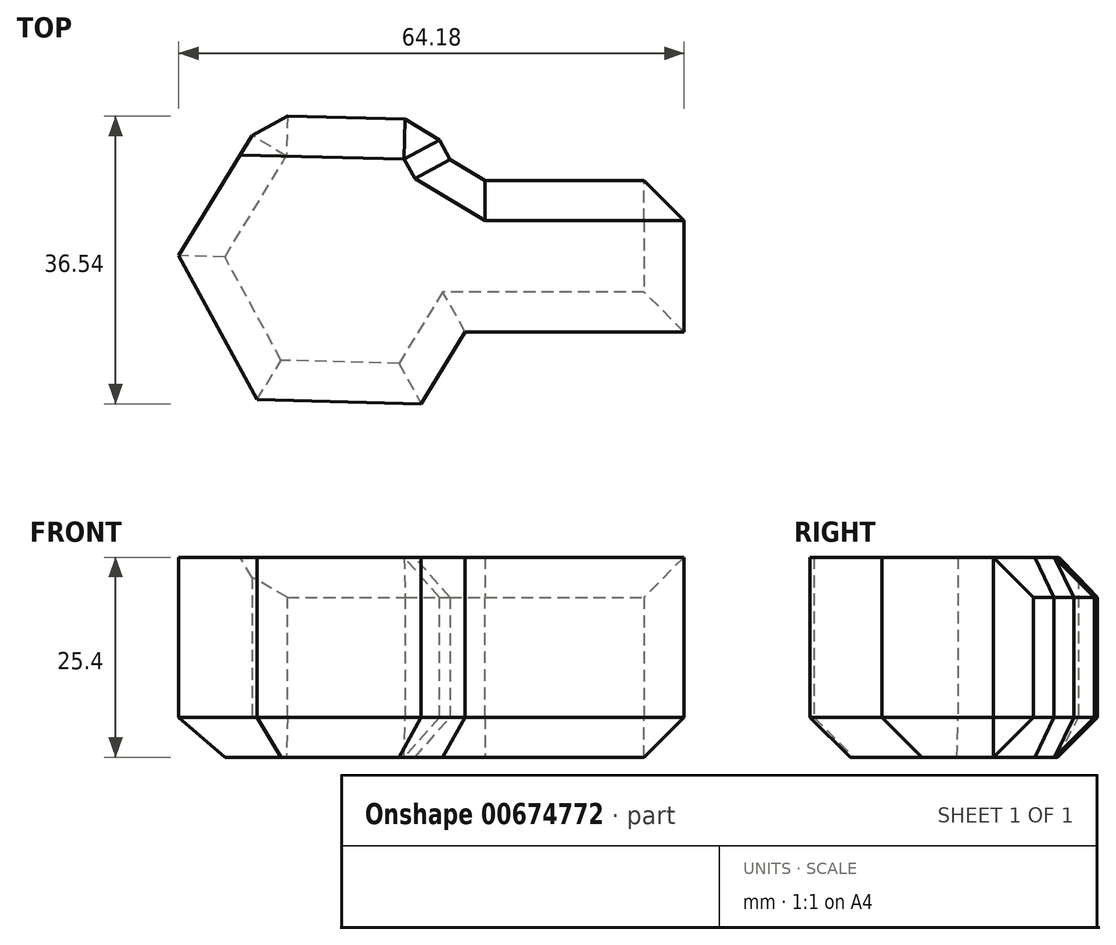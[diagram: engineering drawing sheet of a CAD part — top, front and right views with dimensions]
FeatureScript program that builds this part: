
annotation { "Feature Type Name" : "Feature", "Feature Type Description" : "" }
export const myFeature = defineFeature(function(context is Context, id is Id, definition is map)
    precondition{}
    {
        {
            var Q0;
            Q0=qCreatedBy(makeId("Top.planeOp"),FACE);
            var sketch = newSketch(context, id + "F0", { "sketchPlane" : qUnion([Q0])});
            skCircle(sketch, "E0.cCircle", {"center": v(-46.81, 36.74) * mm, "radius": 18.05 * mm, "construction": true});
            skLineSegment(sketch, "E0.0", {"start": v(-31.26, 27.58) * mm, "end": v(-36.85, 18.43) * mm});
            skLineSegment(sketch, "E0.1", {"start": v(-36.85, 18.43) * mm, "end": v(-57.68, 18.95) * mm});
            skLineSegment(sketch, "E0.2", {"start": v(-57.68, 18.95) * mm, "end": v(-67.65, 37.26) * mm});
            skLineSegment(sketch, "E0.3", {"start": v(-67.65, 37.26) * mm, "end": v(-56.78, 55.04) * mm});
            skLineSegment(sketch, "E0.4", {"start": v(-56.78, 55.04) * mm, "end": v(-35.95, 54.52) * mm});
            skLineSegment(sketch, "E0.5", {"start": v(-35.95, 54.52) * mm, "end": v(-30.96, 45.37) * mm});
            skPoint(sketch, "E0.0.midPoint", {"position": v(-31.41, 27.32) * mm});
            skLineSegment(sketch, "E1.bottom", {"start": v(-31.75, 46.8) * mm, "end": v(-3.47, 46.8) * mm});
            skLineSegment(sketch, "E1.top", {"start": v(-31.75, 27.58) * mm, "end": v(-3.47, 27.58) * mm});
            skLineSegment(sketch, "E1.left", {"start": v(-31.75, 46.8) * mm, "end": v(-31.75, 46.67) * mm});
            skLineSegment(sketch, "E1.right", {"start": v(-3.47, 46.8) * mm, "end": v(-3.47, 27.58) * mm});
            skPoint(sketch, "E2.orphan", {"position": v(-25.98, 36.22) * mm});
            skSolve(sketch);
        }
        {
            var Q0;
            Q0 = qSketchRegion(id + "F0", true);
            extrude(context, id + "F1", {"entities" : qUnion([Q0]), "depth" : 25.4 * mm, "offsetDistance" : 25.4 * mm});
        }
        {
            var Q0;
            Q0=makeQuery(id+"F1.opExtrude","SWEPT_FACE",FACE,{"disambiguationData":[OSD([sQuery(id+"F0.wireOp",EDGE,"E0.4")])]});
            var Q1;
            Q1=makeQuery(id+"F1.opExtrude","SWEPT_FACE",FACE,{"disambiguationData":[OSD([sQuery(id+"F0.wireOp",EDGE,"E0.5")])]});
            var Q2;
            Q2=makeQuery(id+"F1.opExtrude","CAP_EDGE",EDGE,{"disambiguationData":[OSD([sQuery(id+"F0.wireOp",EDGE,"E0.5")])],"isStart":false});
            var Q3;
            Q3=makeQuery(id+"F1.opExtrude","CAP_FACE",FACE,{"disambiguationData":[OSD([sQuery(id+"F0.wireOp",EDGE,"E0.0"),sQuery(id+"F0.wireOp",EDGE,"E0.1"),sQuery(id+"F0.wireOp",EDGE,"E0.2"),sQuery(id+"F0.wireOp",EDGE,"E0.3"),sQuery(id+"F0.wireOp",EDGE,"E0.4"),sQuery(id+"F0.wireOp",EDGE,"E0.5"),sQuery(id+"F0.wireOp",EDGE,"E1.bottom"),sQuery(id+"F0.wireOp",EDGE,"E1.top"),sQuery(id+"F0.wireOp",EDGE,"E1.right")])],"isStart":true});
            var Q4;
            Q4=makeQuery(id+"F1.opExtrude","SWEPT_EDGE",EDGE,{"disambiguationData":[OSD([sQuery(id+"F0.wireOp",EDGE,"E0.4"),sQuery(id+"F0.wireOp",EDGE,"E0.5")])]});
            var Q5;
            Q5=makeQuery(id+"F1.opExtrude","CAP_EDGE",EDGE,{"disambiguationData":[OSD([sQuery(id+"F0.wireOp",EDGE,"E0.4")])],"isStart":false});
            var Q6;
            Q6=makeQuery(id+"F1.opExtrude","CAP_EDGE",EDGE,{"disambiguationData":[OSD([sQuery(id+"F0.wireOp",EDGE,"E0.5")])],"isStart":true});
            var Q7;
            Q7=makeQuery(id+"F1.opExtrude","CAP_EDGE",EDGE,{"disambiguationData":[OSD([sQuery(id+"F0.wireOp",EDGE,"E0.4")])],"isStart":true});
            var Q8;
            Q8=makeQuery(id+"F1.opExtrude","SWEPT_FACE",FACE,{"disambiguationData":[OSD([sQuery(id+"F0.wireOp",EDGE,"E1.bottom")])]});
            var Q9;
            Q9=makeQuery(id+"F1.opExtrude","SWEPT_EDGE",EDGE,{"disambiguationData":[OSD([sQuery(id+"F0.wireOp",EDGE,"E0.5"),sQuery(id+"F0.wireOp",EDGE,"E1.bottom")])]});
            var Q10;
            Q10=makeQuery(id+"F1.opExtrude","CAP_EDGE",EDGE,{"disambiguationData":[OSD([sQuery(id+"F0.wireOp",EDGE,"E1.bottom")])],"isStart":false});
            var Q11;
            Q11=makeQuery(id+"F1.opExtrude","CAP_EDGE",EDGE,{"disambiguationData":[OSD([sQuery(id+"F0.wireOp",EDGE,"E1.bottom")])],"isStart":true});
            chamfer(context, id + "F2", {"entities" : qUnion([Q0, Q1, Q2, Q3, Q4, Q5, Q6, Q7, Q8, Q9, Q10, Q11]), "width" : 5.08 * mm, "tangentPropagation" : true});
        }
    });
